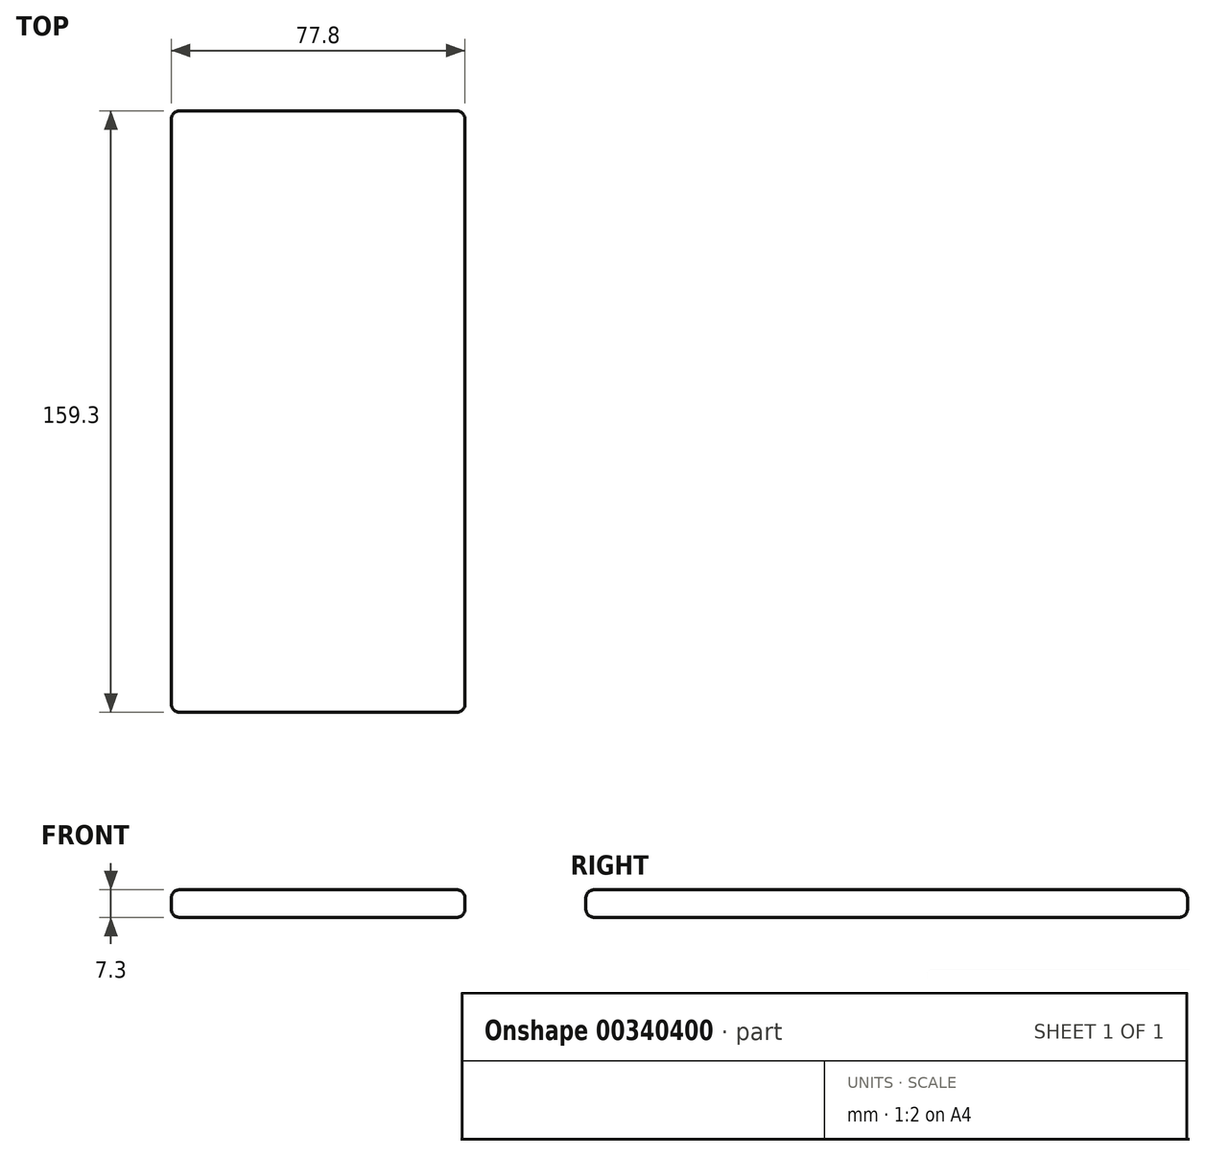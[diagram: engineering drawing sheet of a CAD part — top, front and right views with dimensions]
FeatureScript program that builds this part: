
annotation { "Feature Type Name" : "Feature", "Feature Type Description" : "" }
export const myFeature = defineFeature(function(context is Context, id is Id, definition is map)
    precondition{}
    {
        {
            var Q0;
            Q0=qCreatedBy(makeId("Top.planeOp"),FACE);
            var sketch = newSketch(context, id + "F0", { "sketchPlane" : qUnion([Q0])});
            skLineSegment(sketch, "E0.bottom", {"start": v(38.9, -79.65) * mm, "end": v(-38.9, -79.65) * mm});
            skLineSegment(sketch, "E0.top", {"start": v(38.9, 79.65) * mm, "end": v(-38.9, 79.65) * mm});
            skLineSegment(sketch, "E0.left", {"start": v(38.9, -79.65) * mm, "end": v(38.9, 79.65) * mm});
            skLineSegment(sketch, "E0.right", {"start": v(-38.9, -79.65) * mm, "end": v(-38.9, 79.65) * mm});
            skPoint(sketch, "E0.middle", {"position": v(0, 0) * mm});
            skSolve(sketch);
        }
        {
            var Q0;
            Q0=makeQuery(id+"F0.imprint","IMPRINT",FACE,{"disambiguationData":[TD([[makeQuery(id+"F0.imprint","IMPRINT",EDGE,{"derivedFrom":sQuery(id+"F0.wireOp",EDGE,"E0.bottom")}),-1.0]])]});
            extrude(context, id + "F1", {"entities" : qUnion([Q0]), "depth" : 7.3 * mm});
        }
        {
            var Q0;
            Q0=makeQuery(id+"F1.opExtrude","SWEPT_FACE",FACE,{"disambiguationData":[OSD([sQuery(id+"F0.wireOp",EDGE,"E0.bottom")])]});
            var Q1;
            Q1=makeQuery(id+"F1.opExtrude","SWEPT_FACE",FACE,{"disambiguationData":[OSD([sQuery(id+"F0.wireOp",EDGE,"E0.left")])]});
            var Q2;
            Q2=makeQuery(id+"F1.opExtrude","SWEPT_FACE",FACE,{"disambiguationData":[OSD([sQuery(id+"F0.wireOp",EDGE,"E0.right")])]});
            var Q3;
            Q3=makeQuery(id+"F1.opExtrude","SWEPT_FACE",FACE,{"disambiguationData":[OSD([sQuery(id+"F0.wireOp",EDGE,"E0.top")])]});
            fillet(context, id + "F2", {"entities" : qUnion([Q0, Q1, Q2, Q3]), "radius" : 2.2 * mm, "tangentPropagation" : true, "allowEdgeOverflow" : false});
        }
    });
